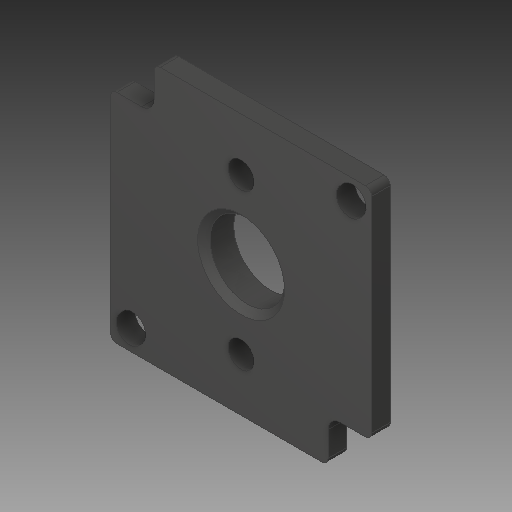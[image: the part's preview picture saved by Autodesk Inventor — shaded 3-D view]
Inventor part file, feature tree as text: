
AUTODESK INVENTOR PART (.ipt)
format: ipt  version: 2017 (Build 210142000, 142)  size: 221,696 bytes
history: native  units: in
note: dims shown in document units (in); Inventor stores cm internally (conversion verified against a paired STEP export)
features: fillet x1
ambient origin geometry x8: Origin, YZ Plane, XZ Plane, XY Plane, X Axis, Y Axis, Z Axis, Center Point
bodies: Solid1 (feature_tree)
feature tree (1):
  fillet  "Fillet4"  [1 undecoded]
note: 1 required parameter value undecoded (feature->parameter linkage not recoverable at this tier; creation-order binding heuristic only, values carry confidence <= 0.55)
